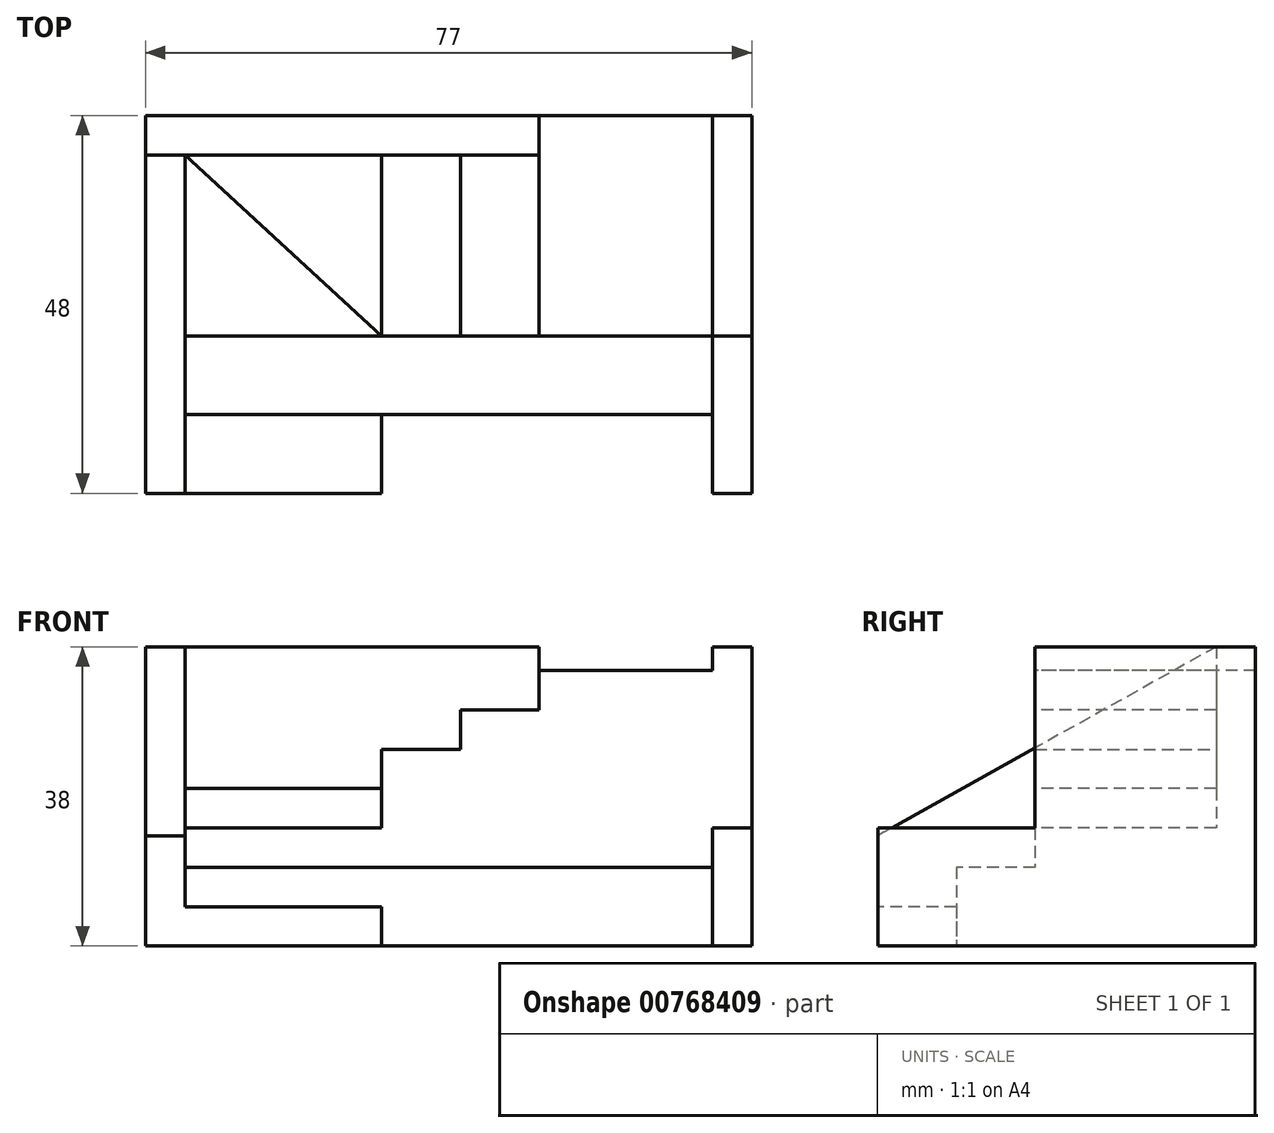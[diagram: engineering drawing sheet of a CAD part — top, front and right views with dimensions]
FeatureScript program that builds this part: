
annotation { "Feature Type Name" : "Feature", "Feature Type Description" : "" }
export const myFeature = defineFeature(function(context is Context, id is Id, definition is map)
    precondition{}
    {
        {
            var Q0;
            Q0=qCreatedBy(makeId("Top.planeOp"),FACE);
            var sketch = newSketch(context, id + "F0", { "sketchPlane" : qUnion([Q0])});
            skLineSegment(sketch, "E0.bottom", {"start": v(-38.5, 24) * mm, "end": v(38.5, 24) * mm});
            skLineSegment(sketch, "E0.top", {"start": v(-38.5, -24) * mm, "end": v(-8.5, -24) * mm});
            skLineSegment(sketch, "E0.left", {"start": v(-38.5, 24) * mm, "end": v(-38.5, -24) * mm});
            skLineSegment(sketch, "E0.right", {"start": v(38.5, 24) * mm, "end": v(38.5, -24) * mm});
            skPoint(sketch, "E0.middle", {"position": v(0, 0) * mm});
            skLineSegment(sketch, "E1", {"start": v(-33.5, 19) * mm, "end": v(-33.5, -24) * mm});
            skLineSegment(sketch, "E2", {"start": v(-38.5, 19) * mm, "end": v(11.5, 19) * mm});
            skLineSegment(sketch, "E3", {"start": v(-33.5, -14) * mm, "end": v(33.5, -14) * mm});
            skLineSegment(sketch, "E4", {"start": v(-33.5, -4) * mm, "end": v(38.5, -4) * mm});
            skPoint(sketch, "E4.endSnap0", {"position": v(38.5, 0) * mm});
            skLineSegment(sketch, "E5", {"start": v(33.5, 24) * mm, "end": v(33.5, -24) * mm});
            skPoint(sketch, "E6.orphan", {"position": v(-38.5, -14) * mm});
            skPoint(sketch, "E7.orphan", {"position": v(-33.5, 24) * mm});
            skPoint(sketch, "E8.orphan", {"position": v(38.5, 19) * mm});
            skLineSegment(sketch, "E9", {"start": v(-8.5, -24) * mm, "end": v(-8.5, -14) * mm});
            skLineSegment(sketch, "E10", {"start": v(-8.5, -4) * mm, "end": v(-8.5, 19) * mm});
            skLineSegment(sketch, "E11", {"start": v(-33.5, 19) * mm, "end": v(-8.5, -4) * mm});
            skLineSegment(sketch, "E12.trimOffspring", {"start": v(33.5, -24) * mm, "end": v(38.5, -24) * mm});
            skLineSegment(sketch, "E13", {"start": v(1.5, 19) * mm, "end": v(1.5, -4) * mm});
            skLineSegment(sketch, "E14", {"start": v(11.5, 19) * mm, "end": v(11.5, -4) * mm});
            skLineSegment(sketch, "E15", {"start": v(11.5, 19) * mm, "end": v(11.5, 24) * mm});
            skSolve(sketch);
        }
        {
            var Q0;
            {var subQ5=sQuery(id+"F0.wireOp",EDGE,"E0.left");var subQ6=sQuery(id+"F0.wireOp",EDGE,"E0.top");var subQ7=makeQuery(id+"F0.imprint","INTERSECT",VERTEX,{"derivedFrom":[subQ6,subQ5]});Q0=makeQuery(id+"F0.imprint","IMPRINT",FACE,{"disambiguationData":[TD([[makeQuery(id+"F0.imprint","IMPRINT",EDGE,{"disambiguationData":[TD([[subQ7,-1.0]])],"derivedFrom":subQ6}),1.0]])]});}
            var Q1;
            {var subQ7=sQuery(id+"F0.wireOp",EDGE,"E15");Q1=makeQuery(id+"F0.imprint","IMPRINT",FACE,{"disambiguationData":[TD([[makeQuery(id+"F0.imprint","IMPRINT",EDGE,{"derivedFrom":subQ7}),1.0]])]});}
            var Q2;
            Q2 = qSketchRegion(id + "F2", true);
            extrude(context, id + "F1", {"entities" : qUnion([Q0, Q1, Q2]), "depth" : 38 * mm, "offsetDistance" : 25 * mm});
        }
        {
            var Q0;
            Q0=makeQuery(id+"F1.opExtrude","SWEPT_FACE",FACE,{"disambiguationData":[OSD([sQuery(id+"F0.wireOp",EDGE,"E1")])]});
            var sketch = newSketch(context, id + "F2", { "sketchPlane" : qUnion([Q0])});
            skLineSegment(sketch, "E16", {"start": v(19, 38) * mm, "end": v(-24, 14) * mm});
            skSolve(sketch);
        }
        {
            var Q0;
            Q0 = qSketchRegion(id + "F2", true);
            var Q1;
            {var subQ0=sQuery(id+"F0.wireOp",EDGE,"E9");Q1=makeQuery(id+"F0.imprint","IMPRINT",FACE,{"disambiguationData":[TD([[makeQuery(id+"F0.imprint","IMPRINT",EDGE,{"derivedFrom":subQ0}),1.0]])]});}
            extrude(context, id + "F3", {"entities" : qUnion([Q0, Q1]), "operationType" : NewBodyOperationType.ADD, "depth" : 5 * mm, "offsetDistance" : 25 * mm});
        }
        {
            var Q0;
            Q0 = qSketchRegion(id + "F2", true);
            var Q1;
            {var subQ1=sQuery(id+"F0.wireOp",EDGE,"E1");var subQ5=sQuery(id+"F0.wireOp",EDGE,"E3");var subQ8=makeQuery(id+"F0.imprint","INTERSECT",VERTEX,{"derivedFrom":[subQ1,subQ5]});Q1=makeQuery(id+"F0.imprint","IMPRINT",FACE,{"disambiguationData":[TD([[makeQuery(id+"F0.imprint","IMPRINT",EDGE,{"disambiguationData":[TD([[subQ8,1.0]])],"derivedFrom":subQ1}),1.0]])]});}
            extrude(context, id + "F4", {"entities" : qUnion([Q0, Q1]), "operationType" : NewBodyOperationType.ADD, "depth" : 10 * mm, "offsetDistance" : 25 * mm});
        }
        {
            var Q0;
            {var subQ0=sQuery(id+"F0.wireOp",EDGE,"E11");Q0=makeQuery(id+"F0.imprint","IMPRINT",FACE,{"disambiguationData":[TD([[makeQuery(id+"F0.imprint","IMPRINT",EDGE,{"derivedFrom":subQ0}),-1.0]])]});}
            extrude(context, id + "F5", {"entities" : qUnion([Q0]), "operationType" : NewBodyOperationType.ADD, "depth" : 15 * mm, "offsetDistance" : 25 * mm});
        }
        {
            var Q0;
            Q0 = qSketchRegion(id + "F2", true);
            var Q1;
            {var subQ2=sQuery(id+"F0.wireOp",EDGE,"E10");Q1=makeQuery(id+"F0.imprint","IMPRINT",FACE,{"disambiguationData":[TD([[makeQuery(id+"F0.imprint","IMPRINT",EDGE,{"derivedFrom":subQ2}),1.0]])]});}
            extrude(context, id + "F6", {"entities" : qUnion([Q0, Q1]), "operationType" : NewBodyOperationType.ADD, "depth" : 20 * mm, "offsetDistance" : 25 * mm});
        }
        {
            var Q0;
            Q0 = qSketchRegion(id + "F2", true);
            var Q1;
            {var subQ0=sQuery(id+"F2.wireOp",EDGE,"E16");Q1=makeQuery(id+"F2.imprint","IMPRINT",FACE,{"disambiguationData":[TD([[makeQuery(id+"F2.imprint","IMPRINT",EDGE,{"derivedFrom":subQ0}),-1.0]])]});}
            extrude(context, id + "F7", {"entities" : qUnion([Q0, Q1]), "operationType" : NewBodyOperationType.REMOVE, "oppositeDirection" : true, "depth" : 25 * mm, "offsetDistance" : 25 * mm});
        }
        {
            var Q0;
            Q0 = qSketchRegion(id + "F2", true);
            var Q1;
            {var subQ0=sQuery(id+"F0.wireOp",EDGE,"E10");Q1=makeQuery(id+"F0.imprint","IMPRINT",FACE,{"disambiguationData":[TD([[makeQuery(id+"F0.imprint","IMPRINT",EDGE,{"derivedFrom":subQ0}),-1.0]])]});}
            extrude(context, id + "F8", {"entities" : qUnion([Q0, Q1]), "operationType" : NewBodyOperationType.ADD, "depth" : 25 * mm, "offsetDistance" : 25 * mm});
        }
        {
            var Q0;
            Q0 = qSketchRegion(id + "F2", true);
            var Q1;
            {var subQ2=sQuery(id+"F0.wireOp",EDGE,"E13");Q1=makeQuery(id+"F0.imprint","IMPRINT",FACE,{"disambiguationData":[TD([[makeQuery(id+"F0.imprint","IMPRINT",EDGE,{"derivedFrom":subQ2}),1.0]])]});}
            extrude(context, id + "F9", {"entities" : qUnion([Q0, Q1]), "operationType" : NewBodyOperationType.ADD, "depth" : 30 * mm, "offsetDistance" : 25 * mm});
        }
        {
            var Q0;
            Q0 = qSketchRegion(id + "F2", true);
            var Q1;
            {var subQ6=sQuery(id+"F0.wireOp",EDGE,"E14");Q1=makeQuery(id+"F0.imprint","IMPRINT",FACE,{"disambiguationData":[TD([[makeQuery(id+"F0.imprint","IMPRINT",EDGE,{"derivedFrom":subQ6}),1.0]])]});}
            extrude(context, id + "F10", {"entities" : qUnion([Q0, Q1]), "operationType" : NewBodyOperationType.ADD, "depth" : 35 * mm, "offsetDistance" : 25 * mm});
        }
        {
            var Q0;
            Q0 = qSketchRegion(id + "F2", true);
            var Q1;
            {var subQ0=sQuery(id+"F0.wireOp",EDGE,"E0.right");var subQ1=sQuery(id+"F0.wireOp",EDGE,"E0.bottom");var subQ2=makeQuery(id+"F0.imprint","INTERSECT",VERTEX,{"derivedFrom":[subQ1,subQ0]});Q1=makeQuery(id+"F0.imprint","IMPRINT",FACE,{"disambiguationData":[TD([[makeQuery(id+"F0.imprint","IMPRINT",EDGE,{"disambiguationData":[TD([[subQ2,1.0]])],"derivedFrom":subQ1}),-1.0]])]});}
            extrude(context, id + "F11", {"entities" : qUnion([Q0, Q1]), "operationType" : NewBodyOperationType.ADD, "depth" : 38 * mm, "offsetDistance" : 25 * mm});
        }
        {
            var Q0;
            Q0 = qSketchRegion(id + "F2", true);
            var Q1;
            {var subQ2=sQuery(id+"F0.wireOp",EDGE,"E12.trimOffspring");Q1=makeQuery(id+"F0.imprint","IMPRINT",FACE,{"disambiguationData":[TD([[makeQuery(id+"F0.imprint","IMPRINT",EDGE,{"derivedFrom":subQ2}),1.0]])]});}
            extrude(context, id + "F12", {"entities" : qUnion([Q0, Q1]), "operationType" : NewBodyOperationType.ADD, "depth" : 15 * mm, "offsetDistance" : 25 * mm});
        }
    });
